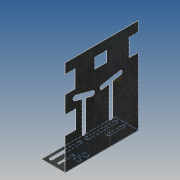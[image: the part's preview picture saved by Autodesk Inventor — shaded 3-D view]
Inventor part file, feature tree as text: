
AUTODESK INVENTOR PART (.ipt)
format: ipt  version: 2016 (Build 200138000, 138)  size: 177,664 bytes
history: native  units: mm
features: extrude x3, sketch x3
ambient origin geometry x8: Origin, YZ Plane, XZ Plane, XY Plane, X Axis, Y Axis, Z Axis, Center Point
bodies: Solid1 (feature_tree)
feature tree (6):
  extrude  "Extrusion1"  Depth=130.0mm
  extrude  "Extrusion2"  Depth=100.0mm TaperAngle=0.0deg
  extrude  "Extrusion5"  Depth=2.5mm
  sketch  "Sketch1"  dims[d0=0.5mm d1=130.0mm]
  sketch  "Sketch2"  dims[d2=32.0mm d3=100.0mm d4=0.0mm]
  sketch  "Sketch5"  dims[d5=100.0mm d6=0.0mm d16=2.5mm d17=10.0mm d18=0.0mm]
